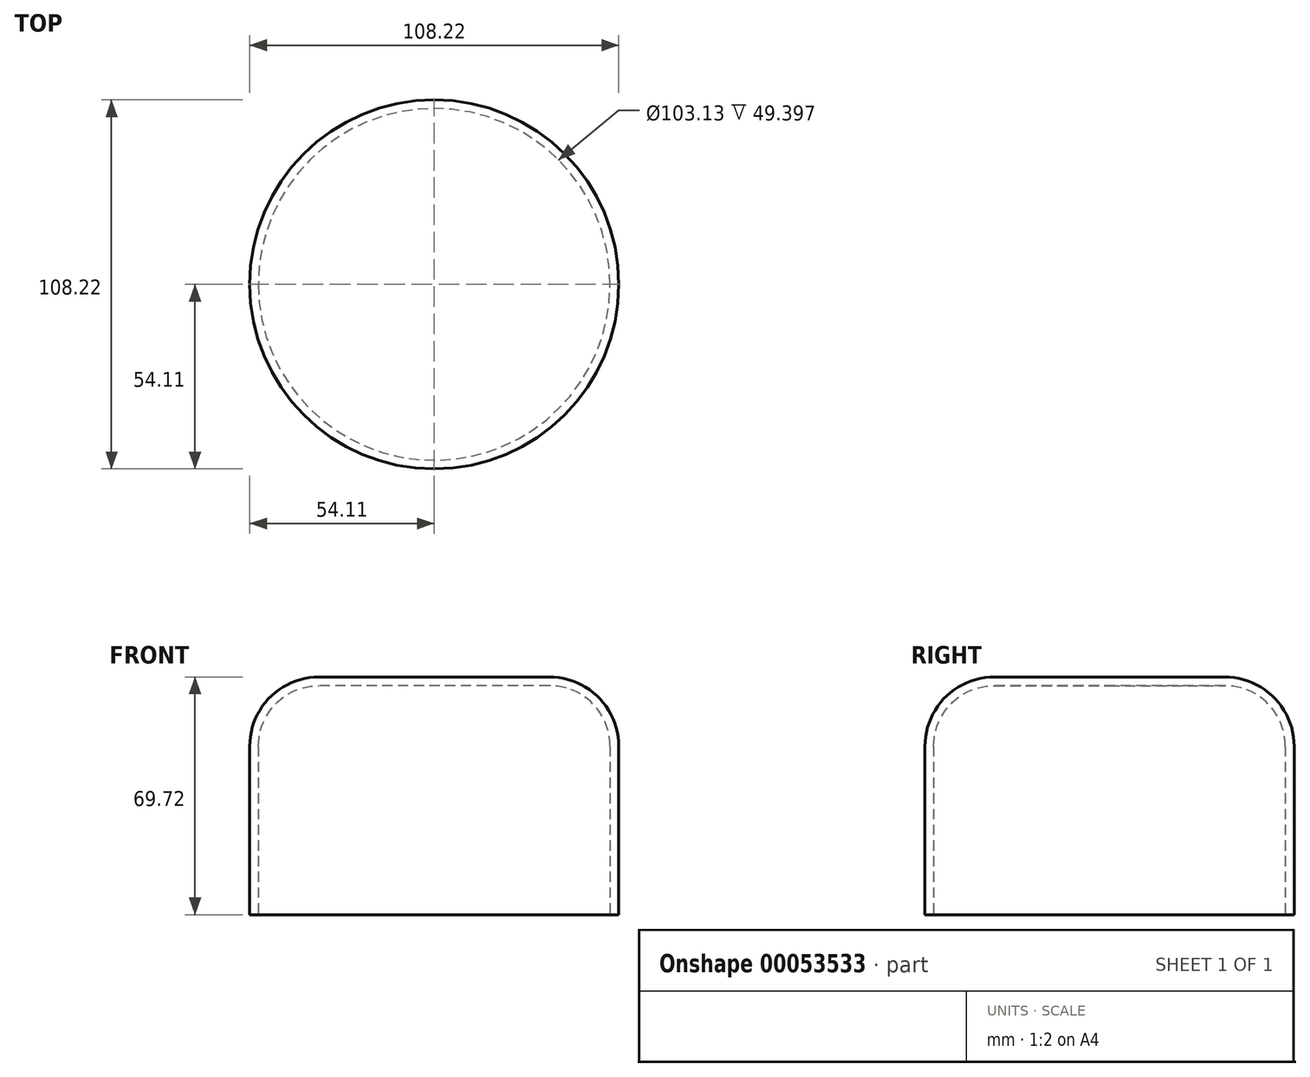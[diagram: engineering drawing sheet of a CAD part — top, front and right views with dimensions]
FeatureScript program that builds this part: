
annotation { "Feature Type Name" : "Feature", "Feature Type Description" : "" }
export const myFeature = defineFeature(function(context is Context, id is Id, definition is map)
    precondition{}
    {
        {
            var Q0;
            Q0=qCreatedBy(makeId("Top.planeOp"),FACE);
            var sketch = newSketch(context, id + "F0", { "sketchPlane" : qUnion([Q0])});
            skCircle(sketch, "E0", {"center": v(0, 0) * mm, "radius": 54.1 * mm});
            skSolve(sketch);
        }
        {
            var Q0;
            Q0 = qSketchRegion(id + "F0", true);
            extrude(context, id + "F1", {"entities" : qUnion([Q0]), "depth" : 69.72 * mm});
        }
        {
            var Q0;
            Q0=makeQuery(id+"F1.opExtrude","CAP_EDGE",EDGE,{"disambiguationData":[OSD([sQuery(id+"F0.wireOp",EDGE,"E0")])],"isStart":false});
            fillet(context, id + "F2", {"entities" : qUnion([Q0]), "radius" : 20.32 * mm, "tangentPropagation" : true, "allowEdgeOverflow" : false});
        }
        {
            var Q0;
            Q0=makeQuery(id+"F1.opExtrude","CAP_FACE",FACE,{"disambiguationData":[OSD([sQuery(id+"F0.wireOp",EDGE,"E0")])],"isStart":true});
            var sketch = newSketch(context, id + "F3", { "sketchPlane" : qUnion([Q0])});
            skCircle(sketch, "E1", {"center": v(0, 0) * mm, "radius": 48.2 * mm});
            skSolve(sketch);
        }
        {
            var Q0;
            Q0=makeQuery(id+"F1.opExtrude","CAP_FACE",FACE,{"disambiguationData":[OSD([sQuery(id+"F0.wireOp",EDGE,"E0")])],"isStart":true});
            shell(context, id + "F4", {"entities" : qUnion([Q0]), "thickness" : 2.54 * mm});
        }
    });
